# Revit family: ПОСТ-РС
name_source: partatom
category: Оборудование
units: mm (PartAtom-declared; Revit-internal decimal feet)

## family parameters
Всегда вертикально = Да
Заголовок OmniClass = Climate Control (HVAC)
На основе рабочей плоскости = Нет
Номер OmniClass = 23.75.00.00
Общий = Нет
При загрузке вырезать с полостями = Нет
Размер круглого соединителя = Использовать диаметр
Тип детали = Нормальный
Точка расчета площади = Нет

## types (15) — shared parameters
ADSK_Единица измерения = шт.
ADSK_Завод-изготовитель = Аэрдин
ADSK_Количество фаз = 3
Data_D = Electric_Drive_Dims
Data_I = DO
Data_S = ПОСТ-РС_s
N = 8
Зонт = Нет
Классификация нагрузок = Вентиляционное оборудование
Материал конфузора = Алюминий, анодированный красный
Материал корпуса = Краска корпуса
Материал рамы = Сталь, окрашенная, синяя
Описание = Радиальный вентилятор низкого давления со спиральным корпусом
zero-valued in all types: Oz, Отметка по умолчанию

## per-type parameters (varying)
| type | A/2 | A1 | C | C1 | C2 | D | Dx | O1 | R | R1 | Re | Wf | Wfr | a1 | a1_2 | a1_4 | a1_4' | d | h |
| ПОСТ-РС-2,5-*-*-* | 88 мм | 190 мм | 86 мм | 260 мм | 260 мм | 250 мм | 350 мм | 105 мм | 125 мм | 140 мм | 155 мм | 15 мм | 50 мм | 175 мм | 88 мм | 44 мм | 46 мм | 7 мм | 305 мм |
| ПОСТ-РС-2,8-*-*-* | 98 мм | 212 мм | 96 мм | 260 мм | 260 мм | 280 мм | 380 мм | 120 мм | 140 мм | 155 мм | 170 мм | 17 мм | 50 мм | 195 мм | 98 мм | 49 мм | 51 мм | 7 мм | 360 мм |
| ПОСТ-РС-3,15-*-*-* | 108 мм | 230 мм | 148 мм | 260 мм | 260 мм | 315 мм | 415 мм | 138 мм | 158 мм | 173 мм | 188 мм | 15 мм | 50 мм | 215 мм | 108 мм | 54 мм | 56 мм | 7 мм | 380 мм |
| ПОСТ-РС-3,55-*-*-* | 125 мм | 264 мм | 155 мм | 340 мм | 340 мм | 355 мм | 455 мм | 158 мм | 178 мм | 193 мм | 205 мм | 15 мм | 50 мм | 249 мм | 125 мм | 62 мм | 64 мм | 7 мм | 430 мм |
| ПОСТ-РС-4,0-*-*-* | 140 мм | 310 мм | 165 мм | 350 мм | 350 мм | 400 мм | 520 мм | 180 мм | 200 мм | 220 мм | 228 мм | 30 мм | 60 мм | 280 мм | 140 мм | 70 мм | 72 мм | 7 мм | 470 мм |
| ПОСТ-РС-4,5-*-*-* | 158 мм | 345 мм | 190 мм | 380 мм | 380 мм | 450 мм | 570 мм | 205 мм | 225 мм | 245 мм | 253 мм | 30 мм | 60 мм | 315 мм | 158 мм | 79 мм | 81 мм | 7 мм | 530 мм |
| ПОСТ-РС-5,0-*-*-* | 174 мм | 380 мм | 211 мм | 410 мм | 410 мм | 500 мм | 620 мм | 220 мм | 250 мм | 270 мм | 278 мм | 32 мм | 60 мм | 348 мм | 174 мм | 87 мм | 89 мм | 7 мм | 575 мм |
| ПОСТ-РС-5,6-*-*-* | 195 мм | 430 мм | 230 мм | 460 мм | 460 мм | 560 мм | 680 мм | 250 мм | 280 мм | 300 мм | 308 мм | 40 мм | 60 мм | 390 мм | 195 мм | 98 мм | 100 мм | 7 мм | 640 мм |
| ПОСТ-РС-6,3-*-*-* | 220 мм | 480 мм | 247 мм | 520 мм | 520 мм | 630 мм | 750 мм | 285 мм | 315 мм | 335 мм | 343 мм | 40 мм | 60 мм | 440 мм | 220 мм | 110 мм | 112 мм | 7 мм | 720 мм |
| ПОСТ-РС-7,1-*-*-* | 248 мм | 530 мм | 280 мм | 590 мм | 590 мм | 710 мм | 910 мм | 315 мм | 355 мм | 375 мм | 383 мм | 35 мм | 100 мм | 495 мм | 248 мм | 124 мм | 126 мм | 7 мм | 805 мм |
| ПОСТ-РС-8,0-*-*-* | 280 мм | 600 мм | 316 мм | 660 мм | 660 мм | 800 мм | 1000 мм | 360 мм | 400 мм | 420 мм | 428 мм | 40 мм | 100 мм | 560 мм | 280 мм | 140 мм | 142 мм | 10 мм | 905 мм |
| ПОСТ-РС-9,0-*-*-* | 315 мм | 670 мм | 340 мм | 720 мм | 720 мм | 900 мм | 1100 мм | 400 мм | 450 мм | 475 мм | 485 мм | 40 мм | 100 мм | 630 мм | 315 мм | 158 мм | 160 мм | 10 мм | 1015 мм |
| ПОСТ-РС-10,0-*-*-* | 350 мм | 750 мм | 360 мм | 840 мм | 840 мм | 1000 мм | 1200 мм | 450 мм | 500 мм | 525 мм | 535 мм | 50 мм | 100 мм | 700 мм | 350 мм | 175 мм | 177 мм | 12 мм | 1130 мм |
| ПОСТ-РС-11,2-*-*-* | 392 мм | 830 мм | 420 мм | 1164 мм | 1164 мм | 1120 мм | 1320 мм | 410 мм | 560 мм | 585 мм | 595 мм | 46 мм | 100 мм | 784 мм | 392 мм | 196 мм | 198 мм | 12 мм | 1235 мм |
| ПОСТ-РС-12,5-*-*-* | 438 мм | 930 мм | 467 мм | 1260 мм | 1260 мм | 1250 мм | 1450 мм | 475 мм | 625 мм | 650 мм | 660 мм | 54 мм | 100 мм | 876 мм | 438 мм | 219 мм | 221 мм | 12 мм | 1380 мм |

## geometry (parser evidence)
native form markers: Blend x14
no freeform markers — native parametric forms only
